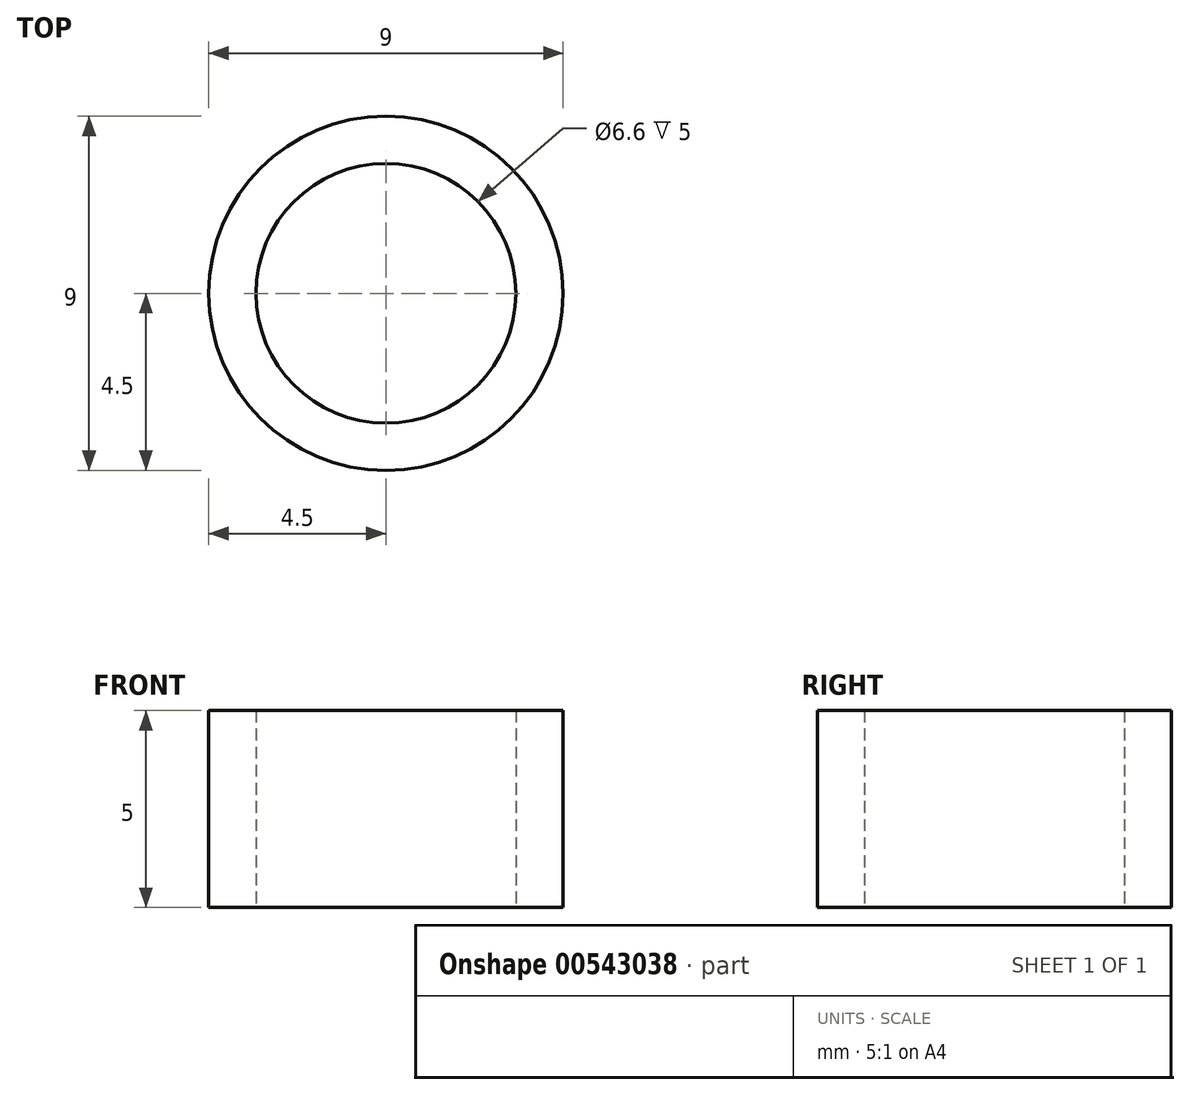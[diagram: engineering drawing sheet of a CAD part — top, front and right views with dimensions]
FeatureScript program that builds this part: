
annotation { "Feature Type Name" : "Feature", "Feature Type Description" : "" }
export const myFeature = defineFeature(function(context is Context, id is Id, definition is map)
    precondition{}
    {
        {
            var Q0;
            Q0=qCreatedBy(makeId("Top.planeOp"),FACE);
            var sketch = newSketch(context, id + "F0", { "sketchPlane" : qUnion([Q0])});
            skCircle(sketch, "E0", {"center": v(0, 0) * mm, "radius": 3.3 * mm});
            skCircle(sketch, "E1", {"center": v(0, 0) * mm, "radius": 4.5 * mm});
            skSolve(sketch);
        }
        {
            var Q0;
            Q0=makeQuery(id+"F0.imprint","IMPRINT",FACE,{"disambiguationData":[TD([[makeQuery(id+"F0.imprint","IMPRINT",EDGE,{"derivedFrom":sQuery(id+"F0.wireOp",EDGE,"E0")}),-1.0]])]});
            extrude(context, id + "F1", {"entities" : qUnion([Q0]), "depth" : 5 * mm, "offsetDistance" : 25 * mm});
        }
    });
